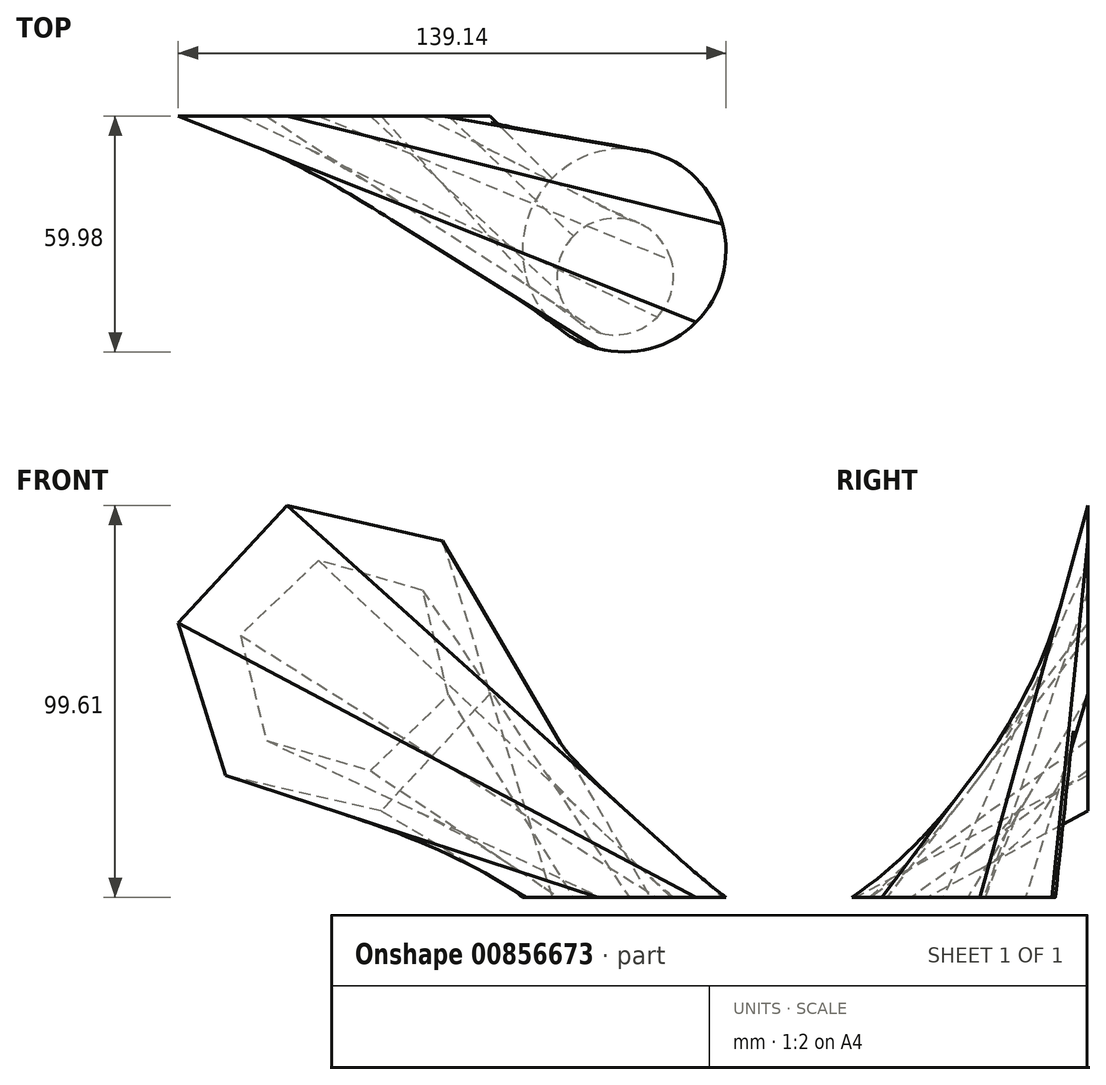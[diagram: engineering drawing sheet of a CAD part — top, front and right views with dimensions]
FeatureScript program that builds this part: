
annotation { "Feature Type Name" : "Feature", "Feature Type Description" : "" }
export const myFeature = defineFeature(function(context is Context, id is Id, definition is map)
    precondition{}
    {
        {
            var Q0;
            Q0=qCreatedBy(makeId("Top.planeOp"),FACE);
            var sketch = newSketch(context, id + "F0", { "sketchPlane" : qUnion([Q0])});
            skCircle(sketch, "E0", {"center": v(47.93, -34.13) * mm, "radius": 25.85 * mm});
            skSolve(sketch);
        }
        {
            var Q0;
            Q0=qCreatedBy(makeId("Front.planeOp"),FACE);
            var sketch = newSketch(context, id + "F1", { "sketchPlane" : qUnion([Q0])});
            skCircle(sketch, "E1.cCircle", {"center": v(-25.78, 60.81) * mm, "radius": 35.16 * mm, "construction": true});
            skLineSegment(sketch, "E1.0", {"start": v(13.8, 51.8) * mm, "end": v(-13.8, 22.02) * mm});
            skLineSegment(sketch, "E1.1", {"start": v(-13.8, 22.02) * mm, "end": v(-53.39, 31.04) * mm});
            skLineSegment(sketch, "E1.2", {"start": v(-53.39, 31.04) * mm, "end": v(-65.37, 69.83) * mm});
            skLineSegment(sketch, "E1.3", {"start": v(-65.37, 69.83) * mm, "end": v(-37.76, 99.6) * mm});
            skLineSegment(sketch, "E1.4", {"start": v(-37.76, 99.6) * mm, "end": v(1.82, 90.58) * mm});
            skLineSegment(sketch, "E1.5", {"start": v(1.82, 90.58) * mm, "end": v(13.8, 51.8) * mm});
            skPoint(sketch, "E1.0.midPoint", {"position": v(0, 36.9) * mm});
            skSolve(sketch);
        }
        {
            var Q0;
            Q0=makeQuery(id+"F1.imprint","IMPRINT",FACE,{"disambiguationData":[TD([[makeQuery(id+"F1.imprint","IMPRINT",EDGE,{"derivedFrom":sQuery(id+"F1.wireOp",EDGE,"E1.0")}),-1.0]])]});
            var Q1;
            Q1=makeQuery(id+"F0.imprint","IMPRINT",FACE,{"disambiguationData":[TD([[makeQuery(id+"F0.imprint","IMPRINT",EDGE,{"derivedFrom":sQuery(id+"F0.wireOp",EDGE,"E0")}),1.0]])]});
            loft(context, id + "F2", {"sheetProfilesArray" : [{ "sheetProfileEntities" : qUnion([Q0]) }, { "sheetProfileEntities" : qUnion([Q1]) }]});
        }
        {
            var Q0;
            Q0=makeQuery(id+"F2.opLoft","CAP_FACE",FACE,{"disambiguationData":[OSD([makeQuery(id+"F1.imprint","IMPRINT",FACE,{"disambiguationData":[TD([[makeQuery(id+"F1.imprint","IMPRINT",EDGE,{"derivedFrom":sQuery(id+"F1.wireOp",EDGE,"E1.0")}),-1.0]])]})])],"isStart":true});
            var sketch = newSketch(context, id + "F3", { "sketchPlane" : qUnion([Q0])});
            skCircle(sketch, "E2.cCircle", {"center": v(23.14, 58.98) * mm, "radius": 23.84 * mm, "construction": true});
            skLineSegment(sketch, "E2.0", {"start": v(-3.3, 51.34) * mm, "end": v(3.3, 78.06) * mm});
            skLineSegment(sketch, "E2.1", {"start": v(3.3, 78.06) * mm, "end": v(29.75, 85.7) * mm});
            skLineSegment(sketch, "E2.2", {"start": v(29.75, 85.7) * mm, "end": v(49.58, 66.62) * mm});
            skLineSegment(sketch, "E2.3", {"start": v(49.58, 66.62) * mm, "end": v(42.98, 39.9) * mm});
            skLineSegment(sketch, "E2.4", {"start": v(42.98, 39.9) * mm, "end": v(16.54, 32.26) * mm});
            skLineSegment(sketch, "E2.5", {"start": v(16.54, 32.26) * mm, "end": v(-3.3, 51.34) * mm});
            skPoint(sketch, "E2.0.midPoint", {"position": v(0, 64.7) * mm});
            skSolve(sketch);
        }
        {
            var Q0;
            Q0=makeQuery(id+"F2.opLoft","CAP_FACE",FACE,{"disambiguationData":[OSD([makeQuery(id+"F0.imprint","IMPRINT",FACE,{"disambiguationData":[TD([[makeQuery(id+"F0.imprint","IMPRINT",EDGE,{"derivedFrom":sQuery(id+"F0.wireOp",EDGE,"E0")}),1.0]])]})])],"isStart":true});
            var sketch = newSketch(context, id + "F4", { "sketchPlane" : qUnion([Q0])});
            skCircle(sketch, "E3", {"center": v(45.65, 40.82) * mm, "radius": 14.82 * mm});
            skSolve(sketch);
        }
        {
            var Q0;
            Q0=makeQuery(id+"F3.imprint","IMPRINT",FACE,{"disambiguationData":[TD([[makeQuery(id+"F3.imprint","IMPRINT",EDGE,{"derivedFrom":sQuery(id+"F3.wireOp",EDGE,"E2.0")}),-1.0]])]});
            var Q1;
            Q1=makeQuery(id+"F4.imprint","IMPRINT",FACE,{"disambiguationData":[TD([[makeQuery(id+"F4.imprint","IMPRINT",EDGE,{"derivedFrom":sQuery(id+"F4.wireOp",EDGE,"E3")}),1.0]])]});
            loft(context, id + "F5", {"operationType" : NewBodyOperationType.REMOVE, "sheetProfilesArray" : [{ "sheetProfileEntities" : qUnion([Q0]) }, { "sheetProfileEntities" : qUnion([Q1]) }]});
        }
    });
